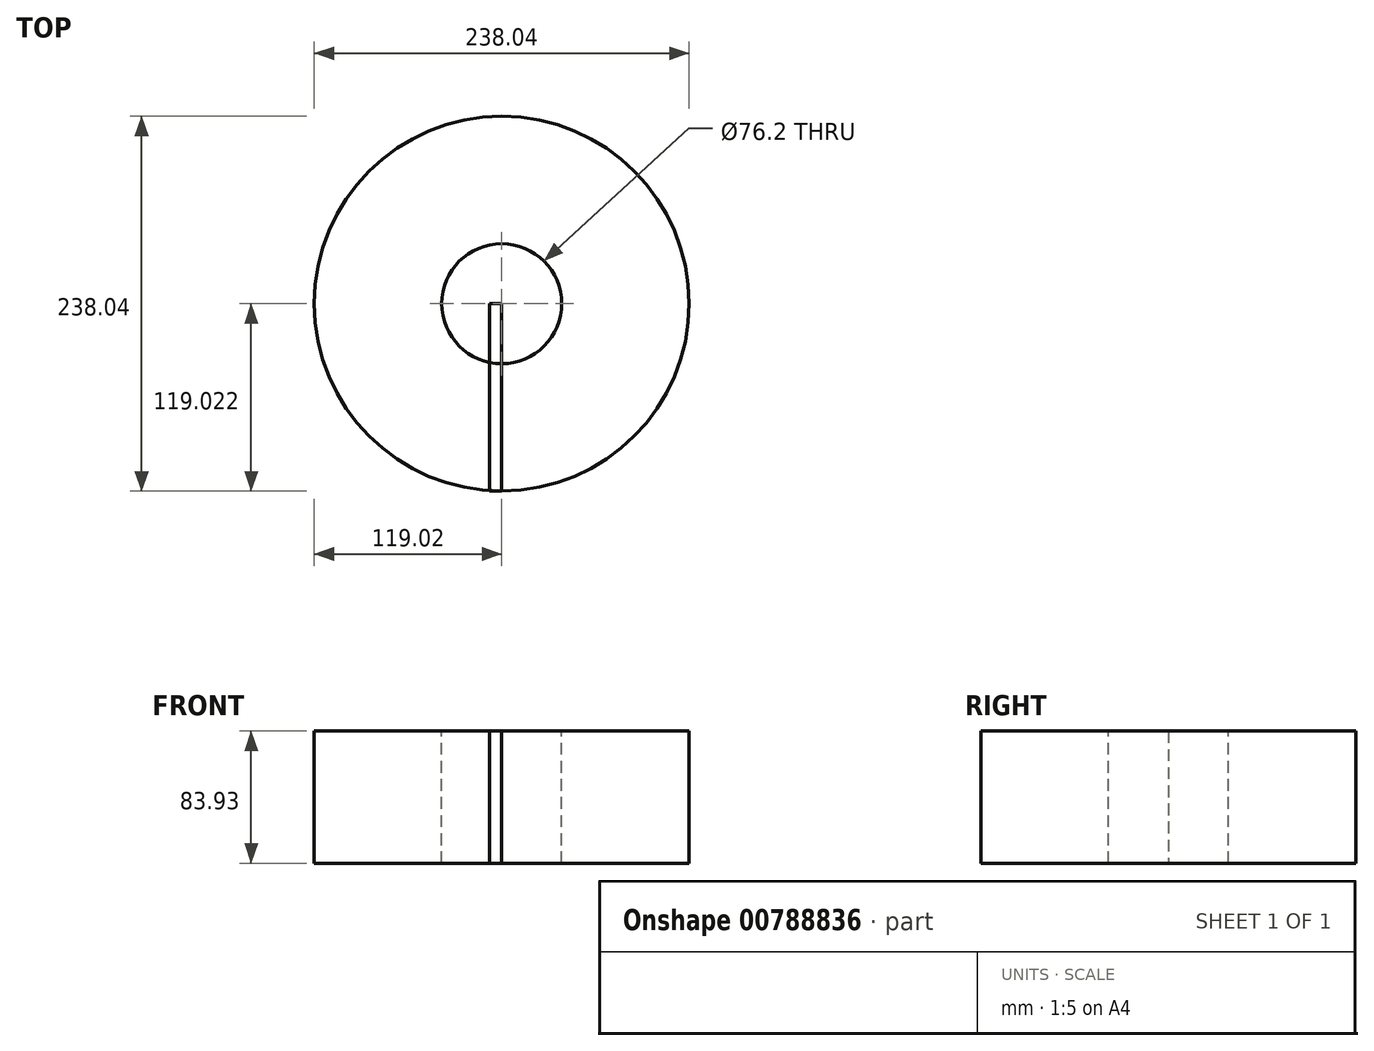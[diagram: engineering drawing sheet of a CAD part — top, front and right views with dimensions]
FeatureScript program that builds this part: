
annotation { "Feature Type Name" : "Feature", "Feature Type Description" : "" }
export const myFeature = defineFeature(function(context is Context, id is Id, definition is map)
    precondition{}
    {
        {
            var Q0;
            Q0=qCreatedBy(makeId("Right.planeOp"),FACE);
            var sketch = newSketch(context, id + "F0", { "sketchPlane" : qUnion([Q0])});
            skLineSegment(sketch, "E0.bottom", {"start": v(-57.56, 41.47) * mm, "end": v(61.46, 41.47) * mm});
            skLineSegment(sketch, "E0.top", {"start": v(-57.56, -42.46) * mm, "end": v(61.46, -42.46) * mm});
            skLineSegment(sketch, "E0.left", {"start": v(-57.56, 41.47) * mm, "end": v(-57.56, -42.46) * mm});
            skLineSegment(sketch, "E0.right", {"start": v(61.46, 41.47) * mm, "end": v(61.46, -42.46) * mm});
            skSolve(sketch);
        }
        {
            var Q0;
            Q0=makeQuery(id+"F0.imprint","IMPRINT",FACE,{"disambiguationData":[TD([[makeQuery(id+"F0.imprint","IMPRINT",EDGE,{"derivedFrom":sQuery(id+"F0.wireOp",EDGE,"E0.bottom")}),-1.0]])]});
            extrude(context, id + "F1", {"entities" : qUnion([Q0]), "depth" : 7.62 * mm, "offsetDistance" : 25.4 * mm});
        }
        {
            var Q0;
            Q0=makeQuery(id+"F1.opExtrude","CAP_FACE",FACE,{"disambiguationData":[OSD([sQuery(id+"F0.wireOp",EDGE,"E0.bottom"),sQuery(id+"F0.wireOp",EDGE,"E0.top"),sQuery(id+"F0.wireOp",EDGE,"E0.left"),sQuery(id+"F0.wireOp",EDGE,"E0.right")])],"isStart":false});
            var Q1;
            Q1=makeQuery(id+"F1.opExtrude","CAP_EDGE",EDGE,{"disambiguationData":[OSD([sQuery(id+"F0.wireOp",EDGE,"E0.right")])],"isStart":false});
            revolve(context, id + "F2", {"surfaceOperationType" : NewSurfaceOperationType.NEW, "entities" : qUnion([Q0]), "axis" : qUnion([Q1]), "revolveType" : RevolveType.ONE_DIRECTION, "angle" : 360 * degree});
        }
        {
            var Q0;
            Q0=makeQuery(id+"F2.opRevolve","SWEPT_FACE",FACE,{"disambiguationData":[OSD([sQuery(id+"F0.wireOp",EDGE,"E0.bottom")])]});
            var sketch = newSketch(context, id + "F3", { "sketchPlane" : qUnion([Q0])});
            skCircle(sketch, "E1", {"center": v(7.62, 61.46) * mm, "radius": 38.06 * mm});
            skSolve(sketch);
        }
        {
            var Q0;
            Q0=sQuery(id+"F3.wireOp",VERTEX,"E1.center");
            var Q1;
            Q1=makeQuery(id+"F2.opRevolve","SWEPT_BODY",BODY,{"disambiguationData":[OSD([sQuery(id+"F0.wireOp",EDGE,"E0.bottom"),sQuery(id+"F0.wireOp",EDGE,"E0.top"),sQuery(id+"F0.wireOp",EDGE,"E0.left"),sQuery(id+"F0.wireOp",EDGE,"E0.right")])]});
            hole(context, id + "F4", {"style" : HoleStyle.SIMPLE, "endStyle" : HoleEndStyle.THROUGH, "holeDiameter" : 76.2 * mm, "majorDiameter" : 6.35 * mm, "isTappedThrough" : true, "tappedDepth" : 12.7 * mm, "tapClearance" : 3, "locations" : qUnion([Q0]), "scope" : qUnion([Q1])});
        }
    });
